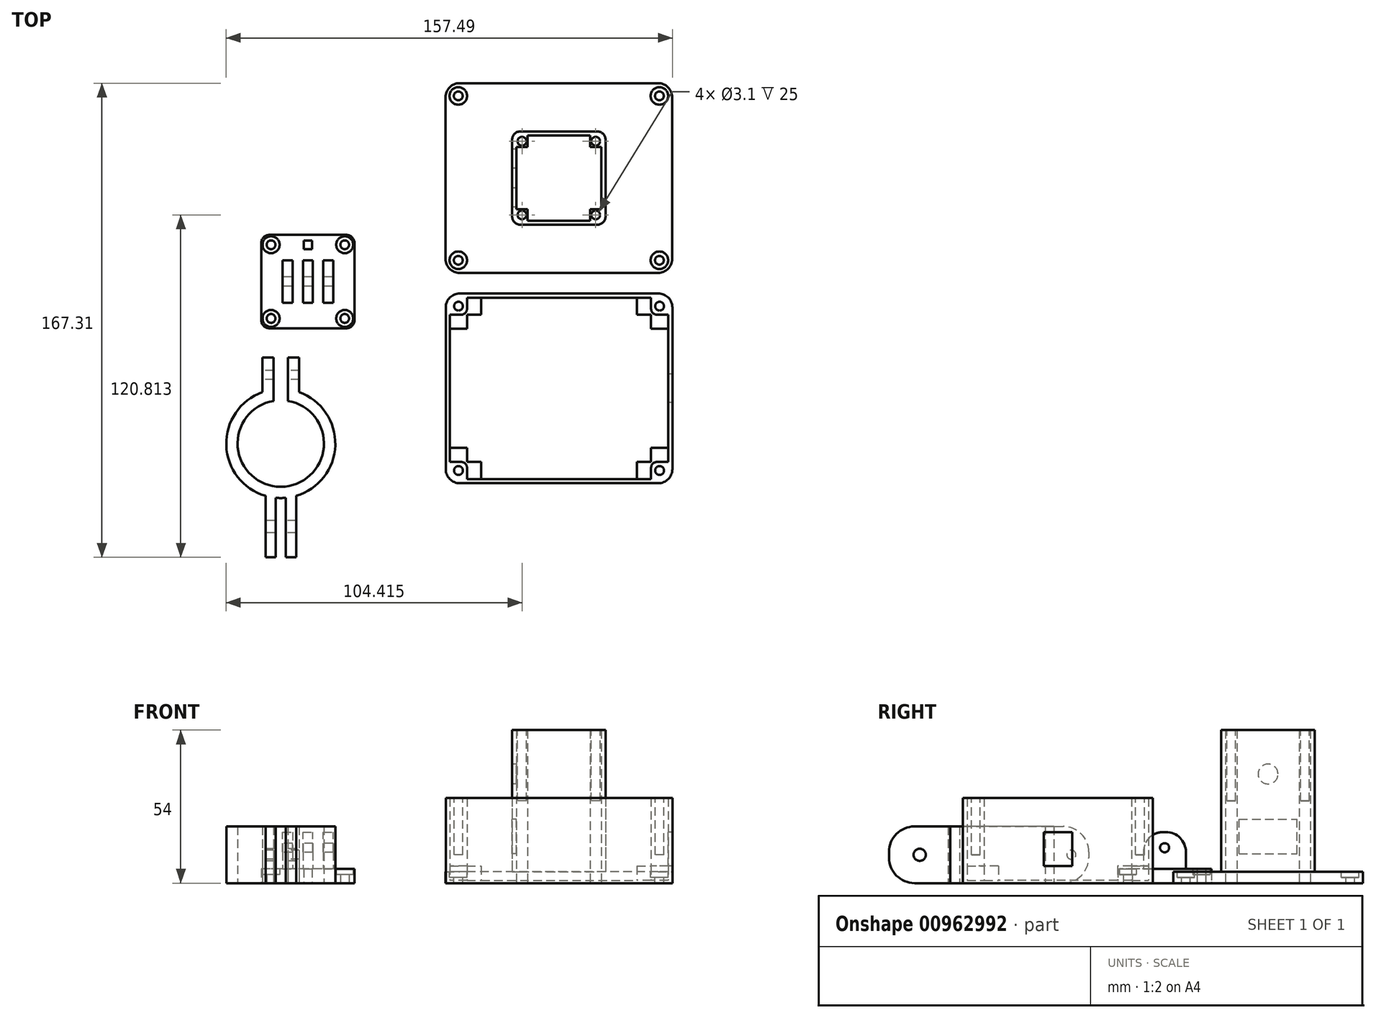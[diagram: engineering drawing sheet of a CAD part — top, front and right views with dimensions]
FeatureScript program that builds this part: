
annotation { "Feature Type Name" : "Feature", "Feature Type Description" : "" }
export const myFeature = defineFeature(function(context is Context, id is Id, definition is map)
    precondition{}
    {
        {
            var Q0;
            Q0=qCreatedBy(makeId("Top.planeOp"),FACE);
            var sketch = newSketch(context, id + "F0", { "sketchPlane" : qUnion([Q0])});
            skLineSegment(sketch, "E0.bottom", {"start": v(-40, 33.5) * mm, "end": v(40, 33.5) * mm});
            skLineSegment(sketch, "E0.top", {"start": v(-40, -33.5) * mm, "end": v(40, -33.5) * mm});
            skLineSegment(sketch, "E0.left", {"start": v(-40, 33.5) * mm, "end": v(-40, -33.5) * mm});
            skLineSegment(sketch, "E0.right", {"start": v(40, 33.5) * mm, "end": v(40, -33.5) * mm});
            skPoint(sketch, "E0.middle", {"position": v(0, 0) * mm});
            skSolve(sketch);
        }
        {
            var Q0;
            Q0 = qSketchRegion(id + "F0", true);
            extrude(context, id + "F1", {"entities" : qUnion([Q0]), "flatOperationType" : FlatOperationType.REMOVE, "depth" : 30 * mm, "offsetDistance" : 25 * mm, "domain" : OperationDomain.MODEL});
        }
        {
            var Q0;
            Q0=makeQuery(id+"F1.opExtrude","CAP_FACE",FACE,{"disambiguationData":[OSD([sQuery(id+"F0.wireOp",EDGE,"E0.bottom"),sQuery(id+"F0.wireOp",EDGE,"E0.top"),sQuery(id+"F0.wireOp",EDGE,"E0.left"),sQuery(id+"F0.wireOp",EDGE,"E0.right")])],"isStart":false});
            var sketch = newSketch(context, id + "F2", { "sketchPlane" : qUnion([Q0])});
            skLineSegment(sketch, "E1.bottom", {"start": v(-38.5, 32) * mm, "end": v(38.5, 32) * mm});
            skLineSegment(sketch, "E1.top", {"start": v(-38.5, -32) * mm, "end": v(38.5, -32) * mm});
            skLineSegment(sketch, "E1.left", {"start": v(-38.5, 32) * mm, "end": v(-38.5, -32) * mm});
            skLineSegment(sketch, "E1.right", {"start": v(38.5, 32) * mm, "end": v(38.5, -32) * mm});
            skPoint(sketch, "E1.middle", {"position": v(0, 0) * mm});
            skSolve(sketch);
        }
        {
            var Q0;
            Q0=makeQuery(id+"F2.imprint","IMPRINT",FACE,{"disambiguationData":[TD([[makeQuery(id+"F2.imprint","IMPRINT",EDGE,{"derivedFrom":sQuery(id+"F2.wireOp",EDGE,"E1.bottom")}),-1.0]])]});
            extrude(context, id + "F3", {"entities" : qUnion([Q0]), "operationType" : NewBodyOperationType.REMOVE, "oppositeDirection" : true, "depth" : 29 * mm, "offsetDistance" : 25 * mm});
        }
        {
            var Q0;
            Q0=makeQuery(id+"F3.boolean.opBoolean","COPY",FACE,{"derivedFrom":makeQuery(id+"F3.opExtrude","CAP_FACE",FACE,{"disambiguationData":[OSD([sQuery(id+"F2.wireOp",EDGE,"E1.bottom"),sQuery(id+"F2.wireOp",EDGE,"E1.top"),sQuery(id+"F2.wireOp",EDGE,"E1.left"),sQuery(id+"F2.wireOp",EDGE,"E1.right")])],"isStart":false})});
            var sketch = newSketch(context, id + "F4", { "sketchPlane" : qUnion([Q0])});
            skLineSegment(sketch, "E2.bottom", {"start": v(-38.5, 32) * mm, "end": v(-32.5, 32) * mm});
            skLineSegment(sketch, "E2.top", {"start": v(-38.5, 26) * mm, "end": v(-32.5, 26) * mm});
            skLineSegment(sketch, "E2.left", {"start": v(-38.5, 32) * mm, "end": v(-38.5, 26) * mm});
            skLineSegment(sketch, "E2.right", {"start": v(-32.5, 32) * mm, "end": v(-32.5, 26) * mm});
            skLineSegment(sketch, "E3.bottom", {"start": v(38.5, 32) * mm, "end": v(32.5, 32) * mm});
            skLineSegment(sketch, "E3.top", {"start": v(38.5, 26) * mm, "end": v(32.5, 26) * mm});
            skLineSegment(sketch, "E3.left", {"start": v(38.5, 32) * mm, "end": v(38.5, 26) * mm});
            skLineSegment(sketch, "E3.right", {"start": v(32.5, 32) * mm, "end": v(32.5, 26) * mm});
            skLineSegment(sketch, "E4.bottom", {"start": v(38.5, -32) * mm, "end": v(32.5, -32) * mm});
            skLineSegment(sketch, "E4.top", {"start": v(38.5, -26) * mm, "end": v(32.5, -26) * mm});
            skLineSegment(sketch, "E4.left", {"start": v(38.5, -32) * mm, "end": v(38.5, -26) * mm});
            skLineSegment(sketch, "E4.right", {"start": v(32.5, -32) * mm, "end": v(32.5, -26) * mm});
            skLineSegment(sketch, "E5.bottom", {"start": v(-38.5, -32) * mm, "end": v(-32.5, -32) * mm});
            skLineSegment(sketch, "E5.top", {"start": v(-38.5, -26) * mm, "end": v(-32.5, -26) * mm});
            skLineSegment(sketch, "E5.left", {"start": v(-38.5, -32) * mm, "end": v(-38.5, -26) * mm});
            skLineSegment(sketch, "E5.right", {"start": v(-32.5, -32) * mm, "end": v(-32.5, -26) * mm});
            skSolve(sketch);
        }
        {
            var Q0;
            Q0 = qSketchRegion(id + "F4", true);
            extrude(context, id + "F5", {"entities" : qUnion([Q0]), "operationType" : NewBodyOperationType.ADD, "depth" : 29 * mm, "offsetDistance" : 25 * mm});
        }
        {
            var Q0;
            Q0=makeQuery(id+"F5.boolean.opBoolean","MERGE",FACE,{"derivedFrom":[makeQuery(id+"F1.opExtrude","CAP_FACE",FACE,{"disambiguationData":[OSD([sQuery(id+"F0.wireOp",EDGE,"E0.bottom"),sQuery(id+"F0.wireOp",EDGE,"E0.top"),sQuery(id+"F0.wireOp",EDGE,"E0.left"),sQuery(id+"F0.wireOp",EDGE,"E0.right")])],"isStart":false}),makeQuery(id+"F5.opExtrude","CAP_FACE",FACE,{"disambiguationData":[OSD([sQuery(id+"F4.wireOp",EDGE,"E2.bottom"),sQuery(id+"F4.wireOp",EDGE,"E2.top"),sQuery(id+"F4.wireOp",EDGE,"E2.left"),sQuery(id+"F4.wireOp",EDGE,"E2.right")])],"isStart":false}),makeQuery(id+"F5.opExtrude","CAP_FACE",FACE,{"disambiguationData":[OSD([sQuery(id+"F4.wireOp",EDGE,"E3.bottom"),sQuery(id+"F4.wireOp",EDGE,"E3.top"),sQuery(id+"F4.wireOp",EDGE,"E3.left"),sQuery(id+"F4.wireOp",EDGE,"E3.right")])],"isStart":false}),makeQuery(id+"F5.opExtrude","CAP_FACE",FACE,{"disambiguationData":[OSD([sQuery(id+"F4.wireOp",EDGE,"E4.bottom"),sQuery(id+"F4.wireOp",EDGE,"E4.top"),sQuery(id+"F4.wireOp",EDGE,"E4.left"),sQuery(id+"F4.wireOp",EDGE,"E4.right")])],"isStart":false}),makeQuery(id+"F5.opExtrude","CAP_FACE",FACE,{"disambiguationData":[OSD([sQuery(id+"F4.wireOp",EDGE,"E5.bottom"),sQuery(id+"F4.wireOp",EDGE,"E5.top"),sQuery(id+"F4.wireOp",EDGE,"E5.left"),sQuery(id+"F4.wireOp",EDGE,"E5.right")])],"isStart":false})]});
            var sketch = newSketch(context, id + "F6", { "sketchPlane" : qUnion([Q0])});
            skCircle(sketch, "E6", {"center": v(35.5, 29) * mm, "radius": 1.55 * mm});
            skPoint(sketch, "E6.centerSnap0", {"position": v(32.5, 29) * mm});
            skPoint(sketch, "E6.centerSnap1", {"position": v(35.5, 26) * mm});
            skCircle(sketch, "E7", {"center": v(35.5, -29) * mm, "radius": 1.55 * mm});
            skPoint(sketch, "E7.centerSnap0", {"position": v(32.5, -29) * mm});
            skCircle(sketch, "E8", {"center": v(-35.5, -29) * mm, "radius": 1.55 * mm});
            skPoint(sketch, "E8.centerSnap0", {"position": v(-35.5, -26) * mm});
            skPoint(sketch, "E8.centerSnap1", {"position": v(-32.5, -29) * mm});
            skCircle(sketch, "E9", {"center": v(-35.5, 29) * mm, "radius": 1.55 * mm});
            skPoint(sketch, "E9.centerSnap0", {"position": v(-32.5, 29) * mm});
            skPoint(sketch, "E9.centerSnap1", {"position": v(-35.5, 26) * mm});
            skSolve(sketch);
        }
        {
            var Q0;
            Q0=makeQuery(id+"F6.imprint","IMPRINT",FACE,{"disambiguationData":[TD([[makeQuery(id+"F6.imprint","IMPRINT",EDGE,{"derivedFrom":sQuery(id+"F6.wireOp",EDGE,"E7")}),1.0]])]});
            var Q1;
            Q1=makeQuery(id+"F6.imprint","IMPRINT",FACE,{"disambiguationData":[TD([[makeQuery(id+"F6.imprint","IMPRINT",EDGE,{"derivedFrom":sQuery(id+"F6.wireOp",EDGE,"E8")}),1.0]])]});
            var Q2;
            Q2=makeQuery(id+"F6.imprint","IMPRINT",FACE,{"disambiguationData":[TD([[makeQuery(id+"F6.imprint","IMPRINT",EDGE,{"derivedFrom":sQuery(id+"F6.wireOp",EDGE,"E9")}),1.0]])]});
            var Q3;
            Q3=makeQuery(id+"F6.imprint","IMPRINT",FACE,{"disambiguationData":[TD([[makeQuery(id+"F6.imprint","IMPRINT",EDGE,{"derivedFrom":sQuery(id+"F6.wireOp",EDGE,"E6")}),1.0]])]});
            extrude(context, id + "F7", {"entities" : qUnion([Q0, Q1, Q2, Q3]), "operationType" : NewBodyOperationType.REMOVE, "oppositeDirection" : true, "depth" : 20 * mm, "offsetDistance" : 25 * mm});
        }
        {
            var Q0;
            Q0=makeQuery(id+"F3.boolean.opBoolean","COPY",FACE,{"derivedFrom":makeQuery(id+"F3.opExtrude","CAP_FACE",FACE,{"disambiguationData":[OSD([sQuery(id+"F2.wireOp",EDGE,"E1.bottom"),sQuery(id+"F2.wireOp",EDGE,"E1.top"),sQuery(id+"F2.wireOp",EDGE,"E1.left"),sQuery(id+"F2.wireOp",EDGE,"E1.right")])],"isStart":false})});
            var sketch = newSketch(context, id + "F8", { "sketchPlane" : qUnion([Q0])});
            skLineSegment(sketch, "E10.bottom", {"start": v(38.5, -26) * mm, "end": v(32.5, -26) * mm});
            skLineSegment(sketch, "E10.top", {"start": v(38.5, -21) * mm, "end": v(32.5, -21) * mm});
            skLineSegment(sketch, "E10.left", {"start": v(38.5, -26) * mm, "end": v(38.5, -21) * mm});
            skLineSegment(sketch, "E10.right", {"start": v(32.5, -26) * mm, "end": v(32.5, -21) * mm});
            skLineSegment(sketch, "E11.bottom", {"start": v(32.5, -32) * mm, "end": v(27.5, -32) * mm});
            skLineSegment(sketch, "E11.top", {"start": v(32.5, -26) * mm, "end": v(27.5, -26) * mm});
            skLineSegment(sketch, "E11.left", {"start": v(32.5, -32) * mm, "end": v(32.5, -26) * mm});
            skLineSegment(sketch, "E11.right", {"start": v(27.5, -32) * mm, "end": v(27.5, -26) * mm});
            skLineSegment(sketch, "E12.bottom", {"start": v(-32.5, -32) * mm, "end": v(-27.5, -32) * mm});
            skLineSegment(sketch, "E12.top", {"start": v(-32.5, -26) * mm, "end": v(-27.5, -26) * mm});
            skLineSegment(sketch, "E12.left", {"start": v(-32.5, -32) * mm, "end": v(-32.5, -26) * mm});
            skLineSegment(sketch, "E12.right", {"start": v(-27.5, -32) * mm, "end": v(-27.5, -26) * mm});
            skLineSegment(sketch, "E13.bottom", {"start": v(-32.5, -26) * mm, "end": v(-38.5, -26) * mm});
            skLineSegment(sketch, "E13.top", {"start": v(-32.5, -21) * mm, "end": v(-38.5, -21) * mm});
            skLineSegment(sketch, "E13.left", {"start": v(-32.5, -26) * mm, "end": v(-32.5, -21) * mm});
            skLineSegment(sketch, "E13.right", {"start": v(-38.5, -26) * mm, "end": v(-38.5, -21) * mm});
            skLineSegment(sketch, "E14.bottom", {"start": v(38.5, 26) * mm, "end": v(32.5, 26) * mm});
            skLineSegment(sketch, "E14.top", {"start": v(38.5, 21) * mm, "end": v(32.5, 21) * mm});
            skLineSegment(sketch, "E14.left", {"start": v(38.5, 26) * mm, "end": v(38.5, 21) * mm});
            skLineSegment(sketch, "E14.right", {"start": v(32.5, 26) * mm, "end": v(32.5, 21) * mm});
            skLineSegment(sketch, "E15.bottom", {"start": v(32.5, 26) * mm, "end": v(27.5, 26) * mm});
            skLineSegment(sketch, "E15.top", {"start": v(32.5, 32) * mm, "end": v(27.5, 32) * mm});
            skLineSegment(sketch, "E15.left", {"start": v(32.5, 26) * mm, "end": v(32.5, 32) * mm});
            skLineSegment(sketch, "E15.right", {"start": v(27.5, 26) * mm, "end": v(27.5, 32) * mm});
            skLineSegment(sketch, "E16.bottom", {"start": v(-32.5, 26) * mm, "end": v(-38.5, 26) * mm});
            skLineSegment(sketch, "E16.top", {"start": v(-32.5, 21) * mm, "end": v(-38.5, 21) * mm});
            skLineSegment(sketch, "E16.left", {"start": v(-32.5, 26) * mm, "end": v(-32.5, 21) * mm});
            skLineSegment(sketch, "E16.right", {"start": v(-38.5, 26) * mm, "end": v(-38.5, 21) * mm});
            skLineSegment(sketch, "E17.bottom", {"start": v(-32.5, 26) * mm, "end": v(-27.5, 26) * mm});
            skLineSegment(sketch, "E17.top", {"start": v(-32.5, 32) * mm, "end": v(-27.5, 32) * mm});
            skLineSegment(sketch, "E17.left", {"start": v(-32.5, 26) * mm, "end": v(-32.5, 32) * mm});
            skLineSegment(sketch, "E17.right", {"start": v(-27.5, 26) * mm, "end": v(-27.5, 32) * mm});
            skSolve(sketch);
        }
        {
            var Q0;
            Q0=makeQuery(id+"F8.imprint","IMPRINT",FACE,{"disambiguationData":[TD([[makeQuery(id+"F8.imprint","IMPRINT",EDGE,{"derivedFrom":sQuery(id+"F8.wireOp",EDGE,"E14.bottom")}),1.0]])]});
            var Q1;
            Q1=makeQuery(id+"F8.imprint","IMPRINT",FACE,{"disambiguationData":[TD([[makeQuery(id+"F8.imprint","IMPRINT",EDGE,{"derivedFrom":sQuery(id+"F8.wireOp",EDGE,"E15.bottom")}),-1.0]])]});
            var Q2;
            Q2=makeQuery(id+"F8.imprint","IMPRINT",FACE,{"disambiguationData":[TD([[makeQuery(id+"F8.imprint","IMPRINT",EDGE,{"derivedFrom":sQuery(id+"F8.wireOp",EDGE,"E10.bottom")}),-1.0]])]});
            var Q3;
            Q3=makeQuery(id+"F8.imprint","IMPRINT",FACE,{"disambiguationData":[TD([[makeQuery(id+"F8.imprint","IMPRINT",EDGE,{"derivedFrom":sQuery(id+"F8.wireOp",EDGE,"E11.bottom")}),1.0]])]});
            var Q4;
            Q4=makeQuery(id+"F8.imprint","IMPRINT",FACE,{"disambiguationData":[TD([[makeQuery(id+"F8.imprint","IMPRINT",EDGE,{"derivedFrom":sQuery(id+"F8.wireOp",EDGE,"E12.bottom")}),1.0]])]});
            var Q5;
            Q5=makeQuery(id+"F8.imprint","IMPRINT",FACE,{"disambiguationData":[TD([[makeQuery(id+"F8.imprint","IMPRINT",EDGE,{"derivedFrom":sQuery(id+"F8.wireOp",EDGE,"E13.bottom")}),1.0]])]});
            var Q6;
            Q6=makeQuery(id+"F8.imprint","IMPRINT",FACE,{"disambiguationData":[TD([[makeQuery(id+"F8.imprint","IMPRINT",EDGE,{"derivedFrom":sQuery(id+"F8.wireOp",EDGE,"E16.bottom")}),-1.0]])]});
            var Q7;
            Q7=makeQuery(id+"F8.imprint","IMPRINT",FACE,{"disambiguationData":[TD([[makeQuery(id+"F8.imprint","IMPRINT",EDGE,{"derivedFrom":sQuery(id+"F8.wireOp",EDGE,"E17.bottom")}),1.0]])]});
            extrude(context, id + "F9", {"entities" : qUnion([Q0, Q1, Q2, Q3, Q4, Q5, Q6, Q7]), "operationType" : NewBodyOperationType.ADD, "depth" : 5 * mm, "offsetDistance" : 25 * mm});
        }
        {
            var Q0;
            Q0=makeQuery(id+"F3.boolean.opBoolean","COPY",FACE,{"derivedFrom":makeQuery(id+"F3.opExtrude","SWEPT_FACE",FACE,{"disambiguationData":[OSD([sQuery(id+"F2.wireOp",EDGE,"E1.right")])]})});
            var sketch = newSketch(context, id + "F10", { "sketchPlane" : qUnion([Q0])});
            skPoint(sketch, "E18.middle.positionSnap0", {"position": v(0, 1) * mm});
            skPoint(sketch, "E18.centerSnap0", {"position": v(0, 1) * mm});
            skPoint(sketch, "E19", {"position": v(-26, 12) * mm});
            skLineSegment(sketch, "E20.bottom", {"start": v(-5, 6) * mm, "end": v(5, 6) * mm});
            skLineSegment(sketch, "E20.top", {"start": v(-5, 18) * mm, "end": v(5, 18) * mm});
            skLineSegment(sketch, "E20.left", {"start": v(-5, 6) * mm, "end": v(-5, 18) * mm});
            skLineSegment(sketch, "E20.right", {"start": v(5, 6) * mm, "end": v(5, 18) * mm});
            skPoint(sketch, "E20.middle", {"position": v(0, 12) * mm});
            skSolve(sketch);
        }
        {
            var Q0;
            Q0=makeQuery(id+"F10.imprint","IMPRINT",FACE,{"disambiguationData":[TD([[makeQuery(id+"F10.imprint","IMPRINT",EDGE,{"derivedFrom":sQuery(id+"F10.wireOp",EDGE,"E20.bottom")}),1.0]])]});
            extrude(context, id + "F11", {"entities" : qUnion([Q0]), "operationType" : NewBodyOperationType.REMOVE, "oppositeDirection" : true, "depth" : 25 * mm, "offsetDistance" : 25 * mm});
        }
        {
            var Q0;
            Q0=makeQuery(id+"F10.imprint","IMPRINT",FACE,{"disambiguationData":[TD([[makeQuery(id+"F10.imprint","IMPRINT",EDGE,{"derivedFrom":sQuery(id+"F10.wireOp",EDGE,"E20.bottom")}),1.0]])]});
            extrude(context, id + "F12", {"entities" : qUnion([Q0]), "operationType" : NewBodyOperationType.REMOVE, "oppositeDirection" : true, "depth" : 25 * mm, "offsetDistance" : 25 * mm});
        }
        {
            var Q0;
            Q0=qCreatedBy(makeId("Top.planeOp"),FACE);
            var sketch = newSketch(context, id + "F13", { "sketchPlane" : qUnion([Q0])});
            skLineSegment(sketch, "E21.bottom", {"start": v(39.93, 40.7) * mm, "end": v(-40.07, 40.7) * mm});
            skLineSegment(sketch, "E21.top", {"start": v(39.93, 107.7) * mm, "end": v(-40.07, 107.7) * mm});
            skLineSegment(sketch, "E21.left", {"start": v(39.93, 40.7) * mm, "end": v(39.93, 107.7) * mm});
            skLineSegment(sketch, "E21.right", {"start": v(-40.07, 40.7) * mm, "end": v(-40.07, 107.7) * mm});
            skSolve(sketch);
        }
        {
            var Q0;
            Q0=makeQuery(id+"F13.imprint","IMPRINT",FACE,{"disambiguationData":[TD([[makeQuery(id+"F13.imprint","IMPRINT",EDGE,{"derivedFrom":sQuery(id+"F13.wireOp",EDGE,"E21.bottom")}),-1.0]])]});
            var Q1;
            Q1 = qSketchRegion(id + "F15", true);
            extrude(context, id + "F14", {"entities" : qUnion([Q0, Q1]), "depth" : 4 * mm, "offsetDistance" : 25 * mm});
        }
        {
            var Q0;
            Q0=makeQuery(id+"F14.opExtrude","CAP_FACE",FACE,{"disambiguationData":[OSD([sQuery(id+"F13.wireOp",EDGE,"E21.bottom"),sQuery(id+"F13.wireOp",EDGE,"E21.top"),sQuery(id+"F13.wireOp",EDGE,"E21.left"),sQuery(id+"F13.wireOp",EDGE,"E21.right")])],"isStart":false});
            var sketch = newSketch(context, id + "F15", { "sketchPlane" : qUnion([Q0])});
            skCircle(sketch, "E22", {"center": v(35.43, 45.2) * mm, "radius": 1.55 * mm});
            skCircle(sketch, "E23", {"center": v(-35.57, 45.2) * mm, "radius": 1.55 * mm});
            skCircle(sketch, "E24", {"center": v(-35.57, 103.2) * mm, "radius": 1.55 * mm});
            skCircle(sketch, "E25", {"center": v(35.43, 103.2) * mm, "radius": 1.55 * mm});
            skSolve(sketch);
        }
        {
            var Q0;
            Q0 = qSketchRegion(id + "F15", true);
            extrude(context, id + "F16", {"entities" : qUnion([Q0]), "operationType" : NewBodyOperationType.REMOVE, "oppositeDirection" : true, "depth" : 25 * mm, "offsetDistance" : 25 * mm});
        }
        {
            var Q0;
            Q0=makeQuery(id+"F14.opExtrude","CAP_FACE",FACE,{"disambiguationData":[OSD([sQuery(id+"F13.wireOp",EDGE,"E21.bottom"),sQuery(id+"F13.wireOp",EDGE,"E21.top"),sQuery(id+"F13.wireOp",EDGE,"E21.left"),sQuery(id+"F13.wireOp",EDGE,"E21.right")])],"isStart":false});
            var sketch = newSketch(context, id + "F17", { "sketchPlane" : qUnion([Q0])});
            skCircle(sketch, "E26", {"center": v(35.43, 45.2) * mm, "radius": 3.1 * mm});
            skCircle(sketch, "E27", {"center": v(-35.57, 45.2) * mm, "radius": 3.1 * mm});
            skCircle(sketch, "E28", {"center": v(-35.57, 103.2) * mm, "radius": 3.1 * mm});
            skCircle(sketch, "E29", {"center": v(35.43, 103.2) * mm, "radius": 3.1 * mm});
            skSolve(sketch);
        }
        {
            var Q0;
            Q0 = qSketchRegion(id + "F17", true);
            extrude(context, id + "F18", {"entities" : qUnion([Q0]), "operationType" : NewBodyOperationType.REMOVE, "oppositeDirection" : true, "depth" : 2 * mm, "offsetDistance" : 25 * mm});
        }
        {
            var Q0;
            Q0=makeQuery(id+"F5.opExtrude","SWEPT_EDGE",EDGE,{"disambiguationData":[OSD([sQuery(id+"F4.wireOp",EDGE,"E4.top"),sQuery(id+"F4.wireOp",EDGE,"E4.right")])]});
            var Q1;
            Q1=makeQuery(id+"F5.opExtrude","SWEPT_EDGE",EDGE,{"disambiguationData":[OSD([sQuery(id+"F4.wireOp",EDGE,"E5.top"),sQuery(id+"F4.wireOp",EDGE,"E5.right")])]});
            var Q2;
            Q2=makeQuery(id+"F5.opExtrude","SWEPT_EDGE",EDGE,{"disambiguationData":[OSD([sQuery(id+"F4.wireOp",EDGE,"E2.top"),sQuery(id+"F4.wireOp",EDGE,"E2.right")])]});
            var Q3;
            Q3=makeQuery(id+"F5.opExtrude","SWEPT_EDGE",EDGE,{"disambiguationData":[OSD([sQuery(id+"F4.wireOp",EDGE,"E3.top"),sQuery(id+"F4.wireOp",EDGE,"E3.right")])]});
            fillet(context, id + "F19", {"entities" : qUnion([Q0, Q1, Q2, Q3]), "radius" : 2 * mm, "tangentPropagation" : true, "allowEdgeOverflow" : false});
        }
        {
            var Q0;
            Q0=makeQuery(id+"F1.opExtrude","SWEPT_EDGE",EDGE,{"disambiguationData":[OSD([sQuery(id+"F0.wireOp",EDGE,"E0.top"),sQuery(id+"F0.wireOp",EDGE,"E0.right")])]});
            var Q1;
            Q1=makeQuery(id+"F1.opExtrude","SWEPT_EDGE",EDGE,{"disambiguationData":[OSD([sQuery(id+"F0.wireOp",EDGE,"E0.top"),sQuery(id+"F0.wireOp",EDGE,"E0.left")])]});
            var Q2;
            Q2=makeQuery(id+"F1.opExtrude","SWEPT_EDGE",EDGE,{"disambiguationData":[OSD([sQuery(id+"F0.wireOp",EDGE,"E0.bottom"),sQuery(id+"F0.wireOp",EDGE,"E0.left")])]});
            var Q3;
            Q3=makeQuery(id+"F1.opExtrude","SWEPT_EDGE",EDGE,{"disambiguationData":[OSD([sQuery(id+"F0.wireOp",EDGE,"E0.bottom"),sQuery(id+"F0.wireOp",EDGE,"E0.right")])]});
            fillet(context, id + "F20", {"entities" : qUnion([Q0, Q1, Q2, Q3]), "radius" : 5 * mm, "tangentPropagation" : true, "allowEdgeOverflow" : false});
        }
        {
            var Q0;
            Q0=makeQuery(id+"F14.opExtrude","SWEPT_EDGE",EDGE,{"disambiguationData":[OSD([sQuery(id+"F13.wireOp",EDGE,"E21.bottom"),sQuery(id+"F13.wireOp",EDGE,"E21.left")])]});
            var Q1;
            Q1=makeQuery(id+"F14.opExtrude","SWEPT_EDGE",EDGE,{"disambiguationData":[OSD([sQuery(id+"F13.wireOp",EDGE,"E21.top"),sQuery(id+"F13.wireOp",EDGE,"E21.left")])]});
            var Q2;
            Q2=makeQuery(id+"F14.opExtrude","SWEPT_EDGE",EDGE,{"disambiguationData":[OSD([sQuery(id+"F13.wireOp",EDGE,"E21.top"),sQuery(id+"F13.wireOp",EDGE,"E21.right")])]});
            var Q3;
            Q3=makeQuery(id+"F14.opExtrude","SWEPT_EDGE",EDGE,{"disambiguationData":[OSD([sQuery(id+"F13.wireOp",EDGE,"E21.bottom"),sQuery(id+"F13.wireOp",EDGE,"E21.right")])]});
            fillet(context, id + "F21", {"entities" : qUnion([Q0, Q1, Q2, Q3]), "radius" : 5 * mm, "tangentPropagation" : true, "allowEdgeOverflow" : false});
        }
        {
            var Q0;
            Q0=makeQuery(id+"F14.opExtrude","CAP_FACE",FACE,{"disambiguationData":[OSD([sQuery(id+"F13.wireOp",EDGE,"E21.bottom"),sQuery(id+"F13.wireOp",EDGE,"E21.top"),sQuery(id+"F13.wireOp",EDGE,"E21.left"),sQuery(id+"F13.wireOp",EDGE,"E21.right")])],"isStart":false});
            var sketch = newSketch(context, id + "F22", { "sketchPlane" : qUnion([Q0])});
            skLineSegment(sketch, "E30.bottom", {"start": v(-15.07, 89.2) * mm, "end": v(14.93, 89.2) * mm});
            skLineSegment(sketch, "E30.top", {"start": v(-15.07, 59.2) * mm, "end": v(14.93, 59.2) * mm});
            skLineSegment(sketch, "E30.left", {"start": v(-15.07, 89.2) * mm, "end": v(-15.07, 59.2) * mm});
            skLineSegment(sketch, "E30.right", {"start": v(14.93, 89.2) * mm, "end": v(14.93, 59.2) * mm});
            skPoint(sketch, "E30.middle", {"position": v(-0.07, 74.2) * mm});
            skPoint(sketch, "E30.middle.positionSnap0", {"position": v(-0.07, 40.7) * mm});
            skPoint(sketch, "E30.middle.positionSnap1", {"position": v(-40.07, 74.2) * mm});
            skPoint(sketch, "E30.centerSnap0", {"position": v(-0.07, 40.7) * mm});
            skPoint(sketch, "E30.centerSnap1", {"position": v(-40.07, 74.2) * mm});
            skLineSegment(sketch, "E31.bottom", {"start": v(-16.57, 57.7) * mm, "end": v(16.43, 57.7) * mm});
            skLineSegment(sketch, "E31.top", {"start": v(-16.57, 90.7) * mm, "end": v(16.43, 90.7) * mm});
            skLineSegment(sketch, "E31.left", {"start": v(-16.57, 57.7) * mm, "end": v(-16.57, 90.7) * mm});
            skLineSegment(sketch, "E31.right", {"start": v(16.43, 57.7) * mm, "end": v(16.43, 90.7) * mm});
            skSolve(sketch);
        }
        {
            var Q0;
            Q0=makeQuery(id+"F22.imprint","IMPRINT",FACE,{"disambiguationData":[TD([[makeQuery(id+"F22.imprint","IMPRINT",EDGE,{"derivedFrom":sQuery(id+"F22.wireOp",EDGE,"E30.bottom")}),-1.0]])]});
            extrude(context, id + "F23", {"entities" : qUnion([Q0]), "operationType" : NewBodyOperationType.REMOVE, "oppositeDirection" : true, "depth" : 25 * mm, "offsetDistance" : 25 * mm});
        }
        {
            var Q0;
            Q0 = qSketchRegion(id + "F22", true);
            extrude(context, id + "F24", {"entities" : qUnion([Q0]), "operationType" : NewBodyOperationType.ADD, "depth" : 50 * mm, "offsetDistance" : 25 * mm});
        }
        {
            var Q0;
            Q0=makeQuery(id+"F14.opExtrude","CAP_FACE",FACE,{"disambiguationData":[OSD([sQuery(id+"F13.wireOp",EDGE,"E21.bottom"),sQuery(id+"F13.wireOp",EDGE,"E21.top"),sQuery(id+"F13.wireOp",EDGE,"E21.left"),sQuery(id+"F13.wireOp",EDGE,"E21.right")])],"isStart":true});
            var sketch = newSketch(context, id + "F25", { "sketchPlane" : qUnion([Q0])});
            skLineSegment(sketch, "E32.bottom", {"start": v(14.93, -89.2) * mm, "end": v(10.93, -89.2) * mm});
            skLineSegment(sketch, "E32.top", {"start": v(14.93, -85.2) * mm, "end": v(10.93, -85.2) * mm});
            skLineSegment(sketch, "E32.left", {"start": v(14.93, -89.2) * mm, "end": v(14.93, -85.2) * mm});
            skLineSegment(sketch, "E32.right", {"start": v(10.93, -89.2) * mm, "end": v(10.93, -85.2) * mm});
            skLineSegment(sketch, "E33.bottom", {"start": v(-15.07, -89.2) * mm, "end": v(-11.07, -89.2) * mm});
            skLineSegment(sketch, "E33.top", {"start": v(-15.07, -85.2) * mm, "end": v(-11.07, -85.2) * mm});
            skLineSegment(sketch, "E33.left", {"start": v(-15.07, -89.2) * mm, "end": v(-15.07, -85.2) * mm});
            skLineSegment(sketch, "E33.right", {"start": v(-11.07, -89.2) * mm, "end": v(-11.07, -85.2) * mm});
            skLineSegment(sketch, "E34.bottom", {"start": v(-15.07, -59.2) * mm, "end": v(-11.07, -59.2) * mm});
            skLineSegment(sketch, "E34.top", {"start": v(-15.07, -63.2) * mm, "end": v(-11.07, -63.2) * mm});
            skLineSegment(sketch, "E34.left", {"start": v(-15.07, -59.2) * mm, "end": v(-15.07, -63.2) * mm});
            skLineSegment(sketch, "E34.right", {"start": v(-11.07, -59.2) * mm, "end": v(-11.07, -63.2) * mm});
            skLineSegment(sketch, "E35.bottom", {"start": v(14.93, -59.2) * mm, "end": v(10.93, -59.2) * mm});
            skLineSegment(sketch, "E35.top", {"start": v(14.93, -63.2) * mm, "end": v(10.93, -63.2) * mm});
            skLineSegment(sketch, "E35.left", {"start": v(14.93, -59.2) * mm, "end": v(14.93, -63.2) * mm});
            skLineSegment(sketch, "E35.right", {"start": v(10.93, -59.2) * mm, "end": v(10.93, -63.2) * mm});
            skSolve(sketch);
        }
        {
            var Q0;
            Q0=makeQuery(id+"F25.imprint","IMPRINT",FACE,{"disambiguationData":[TD([[makeQuery(id+"F25.imprint","IMPRINT",EDGE,{"derivedFrom":sQuery(id+"F25.wireOp",EDGE,"E35.bottom")}),-1.0]])]});
            var Q1;
            Q1=makeQuery(id+"F25.imprint","IMPRINT",FACE,{"disambiguationData":[TD([[makeQuery(id+"F25.imprint","IMPRINT",EDGE,{"derivedFrom":sQuery(id+"F25.wireOp",EDGE,"E34.bottom")}),-1.0]])]});
            var Q2;
            Q2=makeQuery(id+"F25.imprint","IMPRINT",FACE,{"disambiguationData":[TD([[makeQuery(id+"F25.imprint","IMPRINT",EDGE,{"derivedFrom":sQuery(id+"F25.wireOp",EDGE,"E33.bottom")}),1.0]])]});
            var Q3;
            Q3=makeQuery(id+"F25.imprint","IMPRINT",FACE,{"disambiguationData":[TD([[makeQuery(id+"F25.imprint","IMPRINT",EDGE,{"derivedFrom":sQuery(id+"F25.wireOp",EDGE,"E32.bottom")}),1.0]])]});
            extrude(context, id + "F26", {"entities" : qUnion([Q0, Q1, Q2, Q3]), "operationType" : NewBodyOperationType.ADD, "oppositeDirection" : true, "depth" : 54 * mm, "offsetDistance" : 25 * mm});
        }
        {
            var Q0;
            Q0=makeQuery(id+"F26.boolean.opBoolean","MERGE",FACE,{"derivedFrom":[makeQuery(id+"F24.opExtrude","CAP_FACE",FACE,{"disambiguationData":[OSD([sQuery(id+"F22.wireOp",EDGE,"E30.bottom"),sQuery(id+"F22.wireOp",EDGE,"E30.top"),sQuery(id+"F22.wireOp",EDGE,"E30.left"),sQuery(id+"F22.wireOp",EDGE,"E30.right"),sQuery(id+"F22.wireOp",EDGE,"E31.bottom"),sQuery(id+"F22.wireOp",EDGE,"E31.top"),sQuery(id+"F22.wireOp",EDGE,"E31.left"),sQuery(id+"F22.wireOp",EDGE,"E31.right")])],"isStart":false}),makeQuery(id+"F26.opExtrude","CAP_FACE",FACE,{"disambiguationData":[OSD([sQuery(id+"F25.wireOp",EDGE,"E32.bottom"),sQuery(id+"F25.wireOp",EDGE,"E32.top"),sQuery(id+"F25.wireOp",EDGE,"E32.left"),sQuery(id+"F25.wireOp",EDGE,"E32.right")])],"isStart":false}),makeQuery(id+"F26.opExtrude","CAP_FACE",FACE,{"disambiguationData":[OSD([sQuery(id+"F25.wireOp",EDGE,"E33.bottom"),sQuery(id+"F25.wireOp",EDGE,"E33.top"),sQuery(id+"F25.wireOp",EDGE,"E33.left"),sQuery(id+"F25.wireOp",EDGE,"E33.right")])],"isStart":false}),makeQuery(id+"F26.opExtrude","CAP_FACE",FACE,{"disambiguationData":[OSD([sQuery(id+"F25.wireOp",EDGE,"E34.bottom"),sQuery(id+"F25.wireOp",EDGE,"E34.top"),sQuery(id+"F25.wireOp",EDGE,"E34.left"),sQuery(id+"F25.wireOp",EDGE,"E34.right")])],"isStart":false}),makeQuery(id+"F26.opExtrude","CAP_FACE",FACE,{"disambiguationData":[OSD([sQuery(id+"F25.wireOp",EDGE,"E35.bottom"),sQuery(id+"F25.wireOp",EDGE,"E35.top"),sQuery(id+"F25.wireOp",EDGE,"E35.left"),sQuery(id+"F25.wireOp",EDGE,"E35.right")])],"isStart":false})]});
            var sketch = newSketch(context, id + "F27", { "sketchPlane" : qUnion([Q0])});
            skCircle(sketch, "E36", {"center": v(12.93, 61.2) * mm, "radius": 1.55 * mm});
            skPoint(sketch, "E36.centerSnap0", {"position": v(12.93, 63.2) * mm});
            skPoint(sketch, "E36.centerSnap1", {"position": v(10.93, 61.2) * mm});
            skCircle(sketch, "E37", {"center": v(-13.07, 61.2) * mm, "radius": 1.55 * mm});
            skPoint(sketch, "E37.centerSnap0", {"position": v(-11.07, 61.2) * mm});
            skPoint(sketch, "E37.centerSnap1", {"position": v(-13.07, 63.2) * mm});
            skCircle(sketch, "E38", {"center": v(-13.07, 87.2) * mm, "radius": 1.55 * mm});
            skPoint(sketch, "E38.centerSnap0", {"position": v(-11.07, 87.2) * mm});
            skPoint(sketch, "E38.centerSnap1", {"position": v(-13.07, 85.2) * mm});
            skCircle(sketch, "E39", {"center": v(12.93, 87.2) * mm, "radius": 1.55 * mm});
            skPoint(sketch, "E39.centerSnap0", {"position": v(10.93, 87.2) * mm});
            skPoint(sketch, "E39.centerSnap1", {"position": v(12.93, 85.2) * mm});
            skSolve(sketch);
        }
        {
            var Q0;
            Q0=makeQuery(id+"F27.imprint","IMPRINT",FACE,{"disambiguationData":[TD([[makeQuery(id+"F27.imprint","IMPRINT",EDGE,{"derivedFrom":sQuery(id+"F27.wireOp",EDGE,"E36")}),1.0]])]});
            var Q1;
            Q1=makeQuery(id+"F27.imprint","IMPRINT",FACE,{"disambiguationData":[TD([[makeQuery(id+"F27.imprint","IMPRINT",EDGE,{"derivedFrom":sQuery(id+"F27.wireOp",EDGE,"E37")}),1.0]])]});
            var Q2;
            Q2=makeQuery(id+"F27.imprint","IMPRINT",FACE,{"disambiguationData":[TD([[makeQuery(id+"F27.imprint","IMPRINT",EDGE,{"derivedFrom":sQuery(id+"F27.wireOp",EDGE,"E38")}),1.0]])]});
            var Q3;
            Q3=makeQuery(id+"F27.imprint","IMPRINT",FACE,{"disambiguationData":[TD([[makeQuery(id+"F27.imprint","IMPRINT",EDGE,{"derivedFrom":sQuery(id+"F27.wireOp",EDGE,"E39")}),1.0]])]});
            extrude(context, id + "F28", {"entities" : qUnion([Q0, Q1, Q2, Q3]), "operationType" : NewBodyOperationType.REMOVE, "oppositeDirection" : true, "depth" : 25 * mm, "offsetDistance" : 25 * mm});
        }
        {
            var Q0;
            Q0=makeQuery(id+"F24.opExtrude","SWEPT_EDGE",EDGE,{"disambiguationData":[OSD([sQuery(id+"F22.wireOp",EDGE,"E31.top"),sQuery(id+"F22.wireOp",EDGE,"E31.left")])]});
            var Q1;
            Q1=makeQuery(id+"F24.opExtrude","SWEPT_EDGE",EDGE,{"disambiguationData":[OSD([sQuery(id+"F22.wireOp",EDGE,"E31.bottom"),sQuery(id+"F22.wireOp",EDGE,"E31.left")])]});
            var Q2;
            Q2=makeQuery(id+"F24.opExtrude","SWEPT_EDGE",EDGE,{"disambiguationData":[OSD([sQuery(id+"F22.wireOp",EDGE,"E31.top"),sQuery(id+"F22.wireOp",EDGE,"E31.right")])]});
            var Q3;
            Q3=makeQuery(id+"F24.opExtrude","SWEPT_EDGE",EDGE,{"disambiguationData":[OSD([sQuery(id+"F22.wireOp",EDGE,"E31.bottom"),sQuery(id+"F22.wireOp",EDGE,"E31.right")])]});
            fillet(context, id + "F29", {"entities" : qUnion([Q0, Q1, Q2, Q3]), "radius" : 3 * mm, "tangentPropagation" : true, "allowEdgeOverflow" : false});
        }
        {
            var Q0;
            Q0=makeQuery(id+"F24.opExtrude","SWEPT_FACE",FACE,{"disambiguationData":[OSD([sQuery(id+"F22.wireOp",EDGE,"E31.left")])]});
            var sketch = newSketch(context, id + "F30", { "sketchPlane" : qUnion([Q0])});
            skCircle(sketch, "E40", {"center": v(-74.2, 38.5) * mm, "radius": 3.5 * mm});
            skPoint(sketch, "E40.centerSnap0", {"position": v(-74.2, 54) * mm});
            skLineSegment(sketch, "E41.bottom", {"start": v(-63.94, 10.4) * mm, "end": v(-84.44, 10.4) * mm});
            skLineSegment(sketch, "E41.top", {"start": v(-63.94, 22.5) * mm, "end": v(-84.44, 22.5) * mm});
            skLineSegment(sketch, "E41.left", {"start": v(-63.94, 10.4) * mm, "end": v(-63.94, 22.5) * mm});
            skLineSegment(sketch, "E41.right", {"start": v(-84.44, 10.4) * mm, "end": v(-84.44, 22.5) * mm});
            skPoint(sketch, "E41.middle", {"position": v(-74.2, 16.45) * mm});
            skSolve(sketch);
        }
        {
            var Q0;
            Q0=makeQuery(id+"F30.imprint","IMPRINT",FACE,{"disambiguationData":[TD([[makeQuery(id+"F30.imprint","IMPRINT",EDGE,{"derivedFrom":sQuery(id+"F30.wireOp",EDGE,"E41.bottom")}),-1.0]])]});
            var Q1;
            Q1=makeQuery(id+"F30.imprint","IMPRINT",FACE,{"disambiguationData":[TD([[makeQuery(id+"F30.imprint","IMPRINT",EDGE,{"derivedFrom":sQuery(id+"F30.wireOp",EDGE,"E40")}),1.0]])]});
            extrude(context, id + "F31", {"entities" : qUnion([Q0, Q1]), "operationType" : NewBodyOperationType.REMOVE, "oppositeDirection" : true, "depth" : 25 * mm, "offsetDistance" : 25 * mm});
        }
        {
            var Q0;
            Q0=qCreatedBy(makeId("Top.planeOp"),FACE);
            var sketch = newSketch(context, id + "F32", { "sketchPlane" : qUnion([Q0])});
            skLineSegment(sketch, "E42.bottom", {"start": v(-72.17, 54.17) * mm, "end": v(-105.17, 54.17) * mm});
            skLineSegment(sketch, "E42.top", {"start": v(-72.17, 21.17) * mm, "end": v(-105.17, 21.17) * mm});
            skLineSegment(sketch, "E42.left", {"start": v(-72.17, 54.17) * mm, "end": v(-72.17, 21.17) * mm});
            skLineSegment(sketch, "E42.right", {"start": v(-105.17, 54.17) * mm, "end": v(-105.17, 21.17) * mm});
            skCircle(sketch, "E43", {"center": v(-75.67, 50.67) * mm, "radius": 1.55 * mm});
            skCircle(sketch, "E44", {"center": v(-75.67, 24.67) * mm, "radius": 1.55 * mm});
            skCircle(sketch, "E45", {"center": v(-101.67, 24.67) * mm, "radius": 1.55 * mm});
            skCircle(sketch, "E46", {"center": v(-101.67, 50.67) * mm, "radius": 1.55 * mm});
            skLineSegment(sketch, "E47.bottom", {"start": v(-90.17, 49.17) * mm, "end": v(-87.17, 49.17) * mm});
            skLineSegment(sketch, "E47.top", {"start": v(-90.17, 52.17) * mm, "end": v(-87.17, 52.17) * mm});
            skLineSegment(sketch, "E47.left", {"start": v(-90.17, 49.17) * mm, "end": v(-90.17, 52.17) * mm});
            skLineSegment(sketch, "E47.right", {"start": v(-87.17, 49.17) * mm, "end": v(-87.17, 52.17) * mm});
            skPoint(sketch, "E47.middle", {"position": v(-88.67, 50.67) * mm});
            skPoint(sketch, "E47.middle.positionSnap0", {"position": v(-88.67, 54.17) * mm});
            skPoint(sketch, "E47.centerSnap0", {"position": v(-88.67, 54.17) * mm});
            skLineSegment(sketch, "E48.bottom", {"start": v(-97.62, 30.17) * mm, "end": v(-79.72, 30.17) * mm});
            skLineSegment(sketch, "E48.top", {"start": v(-97.62, 45.17) * mm, "end": v(-79.72, 45.17) * mm});
            skLineSegment(sketch, "E48.left", {"start": v(-97.62, 30.17) * mm, "end": v(-97.62, 45.17) * mm});
            skLineSegment(sketch, "E48.right", {"start": v(-79.72, 30.17) * mm, "end": v(-79.72, 45.17) * mm});
            skPoint(sketch, "E48.middle", {"position": v(-88.67, 37.67) * mm});
            skPoint(sketch, "E48.middle.positionSnap0", {"position": v(-88.67, 21.17) * mm});
            skPoint(sketch, "E48.middle.positionSnap1", {"position": v(-72.17, 37.67) * mm});
            skPoint(sketch, "E48.centerSnap0", {"position": v(-88.67, 21.17) * mm});
            skPoint(sketch, "E48.centerSnap1", {"position": v(-72.17, 37.67) * mm});
            skCircle(sketch, "E49", {"center": v(-75.67, 50.67) * mm, "radius": 3 * mm});
            skCircle(sketch, "E50", {"center": v(-75.67, 24.67) * mm, "radius": 3 * mm});
            skCircle(sketch, "E51", {"center": v(-101.67, 24.67) * mm, "radius": 3 * mm});
            skCircle(sketch, "E52", {"center": v(-101.67, 50.67) * mm, "radius": 3 * mm});
            skLineSegment(sketch, "E53.bottom", {"start": v(-86.92, 30.17) * mm, "end": v(-90.42, 30.17) * mm});
            skLineSegment(sketch, "E53.top", {"start": v(-86.92, 45.17) * mm, "end": v(-90.42, 45.17) * mm});
            skLineSegment(sketch, "E53.left", {"start": v(-86.92, 30.17) * mm, "end": v(-86.92, 45.17) * mm});
            skLineSegment(sketch, "E53.right", {"start": v(-90.42, 30.17) * mm, "end": v(-90.42, 45.17) * mm});
            skLineSegment(sketch, "E54.bottom", {"start": v(-97.62, 45.17) * mm, "end": v(-94.12, 45.17) * mm});
            skLineSegment(sketch, "E54.top", {"start": v(-97.62, 30.17) * mm, "end": v(-94.12, 30.17) * mm});
            skLineSegment(sketch, "E54.left", {"start": v(-97.62, 45.17) * mm, "end": v(-97.62, 30.17) * mm});
            skLineSegment(sketch, "E54.right", {"start": v(-94.12, 45.17) * mm, "end": v(-94.12, 30.17) * mm});
            skLineSegment(sketch, "E55.bottom", {"start": v(-79.72, 30.17) * mm, "end": v(-83.22, 30.17) * mm});
            skLineSegment(sketch, "E55.top", {"start": v(-79.72, 45.17) * mm, "end": v(-83.22, 45.17) * mm});
            skLineSegment(sketch, "E55.right", {"start": v(-83.22, 30.17) * mm, "end": v(-83.22, 45.17) * mm});
            skSolve(sketch);
        }
        {
            var Q0;
            Q0=makeQuery(id+"F32.imprint","IMPRINT",FACE,{"disambiguationData":[TD([[makeQuery(id+"F32.imprint","IMPRINT",EDGE,{"derivedFrom":sQuery(id+"F32.wireOp",EDGE,"E42.bottom")}),1.0]])]});
            extrude(context, id + "F33", {"entities" : qUnion([Q0]), "depth" : 5 * mm, "offsetDistance" : 25 * mm});
        }
        {
            var Q0;
            Q0=makeQuery(id+"F32.imprint","IMPRINT",FACE,{"disambiguationData":[TD([[makeQuery(id+"F32.imprint","IMPRINT",EDGE,{"derivedFrom":sQuery(id+"F32.wireOp",EDGE,"E44")}),-1.0]])]});
            var Q1;
            Q1=makeQuery(id+"F32.imprint","IMPRINT",FACE,{"disambiguationData":[TD([[makeQuery(id+"F32.imprint","IMPRINT",EDGE,{"derivedFrom":sQuery(id+"F32.wireOp",EDGE,"E43")}),-1.0]])]});
            var Q2;
            Q2=makeQuery(id+"F32.imprint","IMPRINT",FACE,{"disambiguationData":[TD([[makeQuery(id+"F32.imprint","IMPRINT",EDGE,{"derivedFrom":sQuery(id+"F32.wireOp",EDGE,"E45")}),-1.0]])]});
            var Q3;
            Q3=makeQuery(id+"F32.imprint","IMPRINT",FACE,{"disambiguationData":[TD([[makeQuery(id+"F32.imprint","IMPRINT",EDGE,{"derivedFrom":sQuery(id+"F32.wireOp",EDGE,"E46")}),-1.0]])]});
            extrude(context, id + "F34", {"entities" : qUnion([Q0, Q1, Q2, Q3]), "operationType" : NewBodyOperationType.ADD, "depth" : 3 * mm, "offsetDistance" : 25 * mm});
        }
        {
            var Q0;
            {var subQ0=sQuery(id+"F32.wireOp",EDGE,"E53.left");Q0=makeQuery(id+"F32.imprint","IMPRINT",FACE,{"disambiguationData":[TD([[makeQuery(id+"F32.imprint","IMPRINT",EDGE,{"derivedFrom":subQ0}),-1.0]])]});}
            var Q1;
            {var subQ0=sQuery(id+"F32.wireOp",EDGE,"E53.right");Q1=makeQuery(id+"F32.imprint","IMPRINT",FACE,{"disambiguationData":[TD([[makeQuery(id+"F32.imprint","IMPRINT",EDGE,{"derivedFrom":subQ0}),1.0]])]});}
            extrude(context, id + "F35", {"entities" : qUnion([Q0, Q1]), "operationType" : NewBodyOperationType.ADD, "depth" : 5 * mm, "offsetDistance" : 25 * mm});
        }
        {
            var Q0;
            {var subQ0=sQuery(id+"F32.wireOp",EDGE,"E48.right");Q0=makeQuery(id+"F32.imprint","IMPRINT",FACE,{"disambiguationData":[TD([[makeQuery(id+"F32.imprint","IMPRINT",EDGE,{"derivedFrom":subQ0}),1.0]])]});}
            var Q1;
            {var subQ0=sQuery(id+"F32.wireOp",EDGE,"E53.left");Q1=makeQuery(id+"F32.imprint","IMPRINT",FACE,{"disambiguationData":[TD([[makeQuery(id+"F32.imprint","IMPRINT",EDGE,{"derivedFrom":subQ0}),1.0]])]});}
            var Q2;
            {var subQ0=sQuery(id+"F32.wireOp",EDGE,"E48.left");Q2=makeQuery(id+"F32.imprint","IMPRINT",FACE,{"disambiguationData":[TD([[makeQuery(id+"F32.imprint","IMPRINT",EDGE,{"derivedFrom":subQ0}),-1.0]])]});}
            extrude(context, id + "F36", {"entities" : qUnion([Q0, Q1, Q2]), "operationType" : NewBodyOperationType.ADD, "depth" : 18 * mm, "offsetDistance" : 25 * mm});
        }
        {
            var Q0;
            Q0=makeQuery(id+"F36.opExtrude","SWEPT_FACE",FACE,{"disambiguationData":[OSD([sQuery(id+"F32.wireOp",EDGE,"E48.left")])]});
            var sketch = newSketch(context, id + "F37", { "sketchPlane" : qUnion([Q0])});
            skCircle(sketch, "E56", {"center": v(-37.67, 12.5) * mm, "radius": 1.6 * mm});
            skPoint(sketch, "E56.centerSnap0", {"position": v(-37.67, 18) * mm});
            skSolve(sketch);
        }
        {
            var Q0;
            Q0 = qSketchRegion(id + "F37", true);
            extrude(context, id + "F38", {"entities" : qUnion([Q0]), "operationType" : NewBodyOperationType.REMOVE, "oppositeDirection" : true, "depth" : 25 * mm, "offsetDistance" : 25 * mm});
        }
        {
            var Q0;
            Q0=qCreatedBy(makeId("Top.planeOp"),FACE);
            var sketch = newSketch(context, id + "F39", { "sketchPlane" : qUnion([Q0])});
            skCircle(sketch, "E57", {"center": v(-98.24, -19.48) * mm, "radius": 15.25 * mm});
            skCircle(sketch, "E58", {"center": v(-98.24, -19.48) * mm, "radius": 19.25 * mm});
            skLineSegment(sketch, "E59.bottom", {"start": v(-95.74, -5.14) * mm, "end": v(-100.74, -5.14) * mm});
            skLineSegment(sketch, "E59.top", {"start": v(-95.74, 0.93) * mm, "end": v(-100.74, 0.93) * mm});
            skLineSegment(sketch, "E59.left", {"start": v(-95.74, -5.14) * mm, "end": v(-95.74, 0.93) * mm});
            skLineSegment(sketch, "E59.right", {"start": v(-100.74, -5.14) * mm, "end": v(-100.74, 0.93) * mm});
            skPoint(sketch, "E59.middle", {"position": v(-98.24, -2.1) * mm});
            skLineSegment(sketch, "E60.bottom", {"start": v(-100.74, -2.1) * mm, "end": v(-104.74, -2.1) * mm});
            skLineSegment(sketch, "E60.top", {"start": v(-100.74, 10.9) * mm, "end": v(-104.74, 10.9) * mm});
            skLineSegment(sketch, "E60.left", {"start": v(-100.74, -2.1) * mm, "end": v(-100.74, 10.9) * mm});
            skLineSegment(sketch, "E60.right", {"start": v(-104.74, -2.1) * mm, "end": v(-104.74, 10.9) * mm});
            skLineSegment(sketch, "E61.bottom", {"start": v(-95.74, -2.1) * mm, "end": v(-91.74, -2.1) * mm});
            skLineSegment(sketch, "E61.top", {"start": v(-95.74, 10.9) * mm, "end": v(-91.74, 10.9) * mm});
            skLineSegment(sketch, "E61.left", {"start": v(-95.74, -2.1) * mm, "end": v(-95.74, 10.9) * mm});
            skLineSegment(sketch, "E61.right", {"start": v(-91.74, -2.1) * mm, "end": v(-91.74, 10.9) * mm});
            skLineSegment(sketch, "E62.bottom", {"start": v(-100.04, -34.62) * mm, "end": v(-103.64, -34.62) * mm});
            skLineSegment(sketch, "E62.top", {"start": v(-100.04, -59.62) * mm, "end": v(-103.64, -59.62) * mm});
            skLineSegment(sketch, "E62.left", {"start": v(-100.04, -34.62) * mm, "end": v(-100.04, -59.62) * mm});
            skLineSegment(sketch, "E62.right", {"start": v(-103.64, -34.62) * mm, "end": v(-103.64, -59.62) * mm});
            skLineSegment(sketch, "E63.bottom", {"start": v(-96.44, -34.62) * mm, "end": v(-92.84, -34.62) * mm});
            skLineSegment(sketch, "E63.top", {"start": v(-96.44, -59.62) * mm, "end": v(-92.84, -59.62) * mm});
            skLineSegment(sketch, "E63.left", {"start": v(-96.44, -34.62) * mm, "end": v(-96.44, -59.62) * mm});
            skLineSegment(sketch, "E63.right", {"start": v(-92.84, -34.62) * mm, "end": v(-92.84, -59.62) * mm});
            skSolve(sketch);
        }
        {
            var Q0;
            {var subQ4=sQuery(id+"F39.wireOp",EDGE,"E61.top");Q0=makeQuery(id+"F39.imprint","IMPRINT",FACE,{"disambiguationData":[TD([[makeQuery(id+"F39.imprint","IMPRINT",EDGE,{"derivedFrom":subQ4}),-1.0]])]});}
            var Q1;
            {var subQ2=sQuery(id+"F39.wireOp",EDGE,"E60.top");Q1=makeQuery(id+"F39.imprint","IMPRINT",FACE,{"disambiguationData":[TD([[makeQuery(id+"F39.imprint","IMPRINT",EDGE,{"derivedFrom":subQ2}),1.0]])]});}
            var Q2;
            {var subQ5=sQuery(id+"F39.wireOp",EDGE,"E60.bottom");Q2=makeQuery(id+"F39.imprint","IMPRINT",FACE,{"disambiguationData":[TD([[makeQuery(id+"F39.imprint","IMPRINT",EDGE,{"derivedFrom":subQ5}),-1.0]])]});}
            var Q3;
            {var subQ0=sQuery(id+"F39.wireOp",EDGE,"E60.bottom");Q3=makeQuery(id+"F39.imprint","IMPRINT",FACE,{"disambiguationData":[TD([[makeQuery(id+"F39.imprint","IMPRINT",EDGE,{"derivedFrom":subQ0}),1.0]])]});}
            var Q4;
            {var subQ0=sQuery(id+"F39.wireOp",EDGE,"E61.bottom");Q4=makeQuery(id+"F39.imprint","IMPRINT",FACE,{"disambiguationData":[TD([[makeQuery(id+"F39.imprint","IMPRINT",EDGE,{"derivedFrom":subQ0}),-1.0]])]});}
            var Q5;
            {var subQ5=sQuery(id+"F39.wireOp",EDGE,"E61.bottom");Q5=makeQuery(id+"F39.imprint","IMPRINT",FACE,{"disambiguationData":[TD([[makeQuery(id+"F39.imprint","IMPRINT",EDGE,{"derivedFrom":subQ5}),1.0]])]});}
            var Q6;
            {var subQ5=sQuery(id+"F39.wireOp",EDGE,"E63.bottom");Q6=makeQuery(id+"F39.imprint","IMPRINT",FACE,{"disambiguationData":[TD([[makeQuery(id+"F39.imprint","IMPRINT",EDGE,{"derivedFrom":subQ5}),-1.0]])]});}
            var Q7;
            {var subQ5=sQuery(id+"F39.wireOp",EDGE,"E63.top");Q7=makeQuery(id+"F39.imprint","IMPRINT",FACE,{"disambiguationData":[TD([[makeQuery(id+"F39.imprint","IMPRINT",EDGE,{"derivedFrom":subQ5}),1.0]])]});}
            var Q8;
            {var subQ5=sQuery(id+"F39.wireOp",EDGE,"E62.bottom");Q8=makeQuery(id+"F39.imprint","IMPRINT",FACE,{"disambiguationData":[TD([[makeQuery(id+"F39.imprint","IMPRINT",EDGE,{"derivedFrom":subQ5}),1.0]])]});}
            var Q9;
            {var subQ5=sQuery(id+"F39.wireOp",EDGE,"E62.top");Q9=makeQuery(id+"F39.imprint","IMPRINT",FACE,{"disambiguationData":[TD([[makeQuery(id+"F39.imprint","IMPRINT",EDGE,{"derivedFrom":subQ5}),-1.0]])]});}
            var Q10;
            {var subQ0=sQuery(id+"F39.wireOp",EDGE,"E62.left");var subQ5=sQuery(id+"F39.wireOp",EDGE,"E58");var subQ6=makeQuery(id+"F39.imprint","INTERSECT",VERTEX,{"derivedFrom":[subQ5,subQ0]});Q10=makeQuery(id+"F39.imprint","IMPRINT",FACE,{"disambiguationData":[TD([[makeQuery(id+"F39.imprint","IMPRINT",EDGE,{"disambiguationData":[TD([[subQ6,-1.0]])],"derivedFrom":subQ5}),1.0]])]});}
            extrude(context, id + "F40", {"entities" : qUnion([Q0, Q1, Q2, Q3, Q4, Q5, Q6, Q7, Q8, Q9, Q10]), "depth" : 20 * mm, "offsetDistance" : 25 * mm});
        }
        {
            var Q0;
            Q0=makeQuery(id+"F40.opExtrude","SWEPT_FACE",FACE,{"disambiguationData":[OSD([sQuery(id+"F39.wireOp",EDGE,"E62.right")])]});
            var sketch = newSketch(context, id + "F41", { "sketchPlane" : qUnion([Q0])});
            skCircle(sketch, "E64", {"center": v(48.79, 10) * mm, "radius": 2.15 * mm});
            skPoint(sketch, "E64.centerSnap0", {"position": v(48.79, 20) * mm});
            skPoint(sketch, "E64.centerSnap1", {"position": v(59.62, 10) * mm});
            skSolve(sketch);
        }
        {
            var Q0;
            Q0=makeQuery(id+"F41.imprint","IMPRINT",FACE,{"disambiguationData":[TD([[makeQuery(id+"F41.imprint","IMPRINT",EDGE,{"derivedFrom":sQuery(id+"F41.wireOp",EDGE,"E64")}),1.0]])]});
            extrude(context, id + "F42", {"entities" : qUnion([Q0]), "operationType" : NewBodyOperationType.REMOVE, "oppositeDirection" : true, "depth" : 25 * mm, "offsetDistance" : 25 * mm});
        }
        {
            var Q0;
            Q0=makeQuery(id+"F40.opExtrude","SWEPT_FACE",FACE,{"disambiguationData":[OSD([sQuery(id+"F39.wireOp",EDGE,"E60.right")])]});
            var sketch = newSketch(context, id + "F43", { "sketchPlane" : qUnion([Q0])});
            skCircle(sketch, "E65", {"center": v(-4.77, 10) * mm, "radius": 1.6 * mm});
            skPoint(sketch, "E65.centerSnap0", {"position": v(-4.77, 20) * mm});
            skPoint(sketch, "E65.centerSnap1", {"position": v(-10.9, 10) * mm});
            skSolve(sketch);
        }
        {
            var Q0;
            Q0=makeQuery(id+"F43.imprint","IMPRINT",FACE,{"disambiguationData":[TD([[makeQuery(id+"F43.imprint","IMPRINT",EDGE,{"derivedFrom":sQuery(id+"F43.wireOp",EDGE,"E65")}),1.0]])]});
            extrude(context, id + "F44", {"entities" : qUnion([Q0]), "operationType" : NewBodyOperationType.REMOVE, "oppositeDirection" : true, "depth" : 25 * mm, "offsetDistance" : 25 * mm});
        }
        {
            var Q0;
            Q0=makeQuery(id+"F40.opExtrude","CAP_EDGE",EDGE,{"disambiguationData":[OSD([sQuery(id+"F39.wireOp",EDGE,"E62.top")])],"isStart":false});
            var Q1;
            Q1=makeQuery(id+"F40.opExtrude","CAP_EDGE",EDGE,{"disambiguationData":[OSD([sQuery(id+"F39.wireOp",EDGE,"E63.top")])],"isStart":false});
            var Q2;
            Q2=makeQuery(id+"F40.opExtrude","CAP_EDGE",EDGE,{"disambiguationData":[OSD([sQuery(id+"F39.wireOp",EDGE,"E62.top")])],"isStart":true});
            var Q3;
            Q3=makeQuery(id+"F40.opExtrude","CAP_EDGE",EDGE,{"disambiguationData":[OSD([sQuery(id+"F39.wireOp",EDGE,"E63.top")])],"isStart":true});
            var Q4;
            Q4=makeQuery(id+"F40.opExtrude","CAP_EDGE",EDGE,{"disambiguationData":[OSD([sQuery(id+"F39.wireOp",EDGE,"E60.top")])],"isStart":false});
            var Q5;
            Q5=makeQuery(id+"F40.opExtrude","CAP_EDGE",EDGE,{"disambiguationData":[OSD([sQuery(id+"F39.wireOp",EDGE,"E61.top")])],"isStart":false});
            var Q6;
            Q6=makeQuery(id+"F40.opExtrude","CAP_EDGE",EDGE,{"disambiguationData":[OSD([sQuery(id+"F39.wireOp",EDGE,"E61.top")])],"isStart":true});
            var Q7;
            Q7=makeQuery(id+"F40.opExtrude","CAP_EDGE",EDGE,{"disambiguationData":[OSD([sQuery(id+"F39.wireOp",EDGE,"E60.top")])],"isStart":true});
            fillet(context, id + "F45", {"entities" : qUnion([Q0, Q1, Q2, Q3, Q4, Q5, Q6, Q7]), "radius" : 9 * mm, "tangentPropagation" : true, "allowEdgeOverflow" : false});
        }
        {
            var Q0;
            {var subQ0=sQuery(id+"F32.wireOp",EDGE,"E48.top");Q0=makeQuery(id+"F36.opExtrude","CAP_EDGE",EDGE,{"disambiguationData":[OSD([subQ0]),TDD([makeQuery(id+"F32.imprint","IMPRINT",EDGE,{"disambiguationData":[TD([[makeQuery(id+"F32.imprint","INTERSECT",VERTEX,{"derivedFrom":[subQ0,sQuery(id+"F32.wireOp",EDGE,"E48.left")]}),-1.0]])],"derivedFrom":subQ0})])],"isStart":false});}
            var Q1;
            {var subQ0=sQuery(id+"F32.wireOp",EDGE,"E48.top");Q1=makeQuery(id+"F36.opExtrude","CAP_EDGE",EDGE,{"disambiguationData":[OSD([subQ0]),TDD([makeQuery(id+"F32.imprint","IMPRINT",EDGE,{"disambiguationData":[TD([[makeQuery(id+"F32.imprint","INTERSECT",VERTEX,{"derivedFrom":[subQ0,sQuery(id+"F32.wireOp",EDGE,"E53.left")]}),1.0]])],"derivedFrom":subQ0})])],"isStart":false});}
            var Q2;
            {var subQ0=sQuery(id+"F32.wireOp",EDGE,"E48.top");Q2=makeQuery(id+"F36.opExtrude","CAP_EDGE",EDGE,{"disambiguationData":[OSD([subQ0]),TDD([makeQuery(id+"F32.imprint","IMPRINT",EDGE,{"disambiguationData":[TD([[makeQuery(id+"F32.imprint","INTERSECT",VERTEX,{"derivedFrom":[subQ0,sQuery(id+"F32.wireOp",EDGE,"E48.right")]}),1.0]])],"derivedFrom":subQ0})])],"isStart":false});}
            var Q3;
            {var subQ0=sQuery(id+"F32.wireOp",EDGE,"E48.bottom");Q3=makeQuery(id+"F36.opExtrude","CAP_EDGE",EDGE,{"disambiguationData":[OSD([subQ0]),TDD([makeQuery(id+"F32.imprint","IMPRINT",EDGE,{"disambiguationData":[TD([[makeQuery(id+"F32.imprint","INTERSECT",VERTEX,{"derivedFrom":[subQ0,sQuery(id+"F32.wireOp",EDGE,"E48.right")]}),1.0]])],"derivedFrom":subQ0})])],"isStart":false});}
            var Q4;
            {var subQ0=sQuery(id+"F32.wireOp",EDGE,"E48.bottom");Q4=makeQuery(id+"F36.opExtrude","CAP_EDGE",EDGE,{"disambiguationData":[OSD([subQ0]),TDD([makeQuery(id+"F32.imprint","IMPRINT",EDGE,{"disambiguationData":[TD([[makeQuery(id+"F32.imprint","INTERSECT",VERTEX,{"derivedFrom":[subQ0,sQuery(id+"F32.wireOp",EDGE,"E53.left")]}),1.0]])],"derivedFrom":subQ0})])],"isStart":false});}
            var Q5;
            {var subQ0=sQuery(id+"F32.wireOp",EDGE,"E48.bottom");Q5=makeQuery(id+"F36.opExtrude","CAP_EDGE",EDGE,{"disambiguationData":[OSD([subQ0]),TDD([makeQuery(id+"F32.imprint","IMPRINT",EDGE,{"disambiguationData":[TD([[makeQuery(id+"F32.imprint","INTERSECT",VERTEX,{"derivedFrom":[subQ0,sQuery(id+"F32.wireOp",EDGE,"E48.left")]}),-1.0]])],"derivedFrom":subQ0})])],"isStart":false});}
            fillet(context, id + "F46", {"entities" : qUnion([Q0, Q1, Q2, Q3, Q4, Q5]), "radius" : 7 * mm, "tangentPropagation" : true, "allowEdgeOverflow" : false});
        }
        {
            var Q0;
            Q0=makeQuery(id+"F33.opExtrude","SWEPT_EDGE",EDGE,{"disambiguationData":[OSD([sQuery(id+"F32.wireOp",EDGE,"E42.bottom"),sQuery(id+"F32.wireOp",EDGE,"E42.left")])]});
            var Q1;
            Q1=makeQuery(id+"F33.opExtrude","SWEPT_EDGE",EDGE,{"disambiguationData":[OSD([sQuery(id+"F32.wireOp",EDGE,"E42.bottom"),sQuery(id+"F32.wireOp",EDGE,"E42.right")])]});
            var Q2;
            Q2=makeQuery(id+"F33.opExtrude","SWEPT_EDGE",EDGE,{"disambiguationData":[OSD([sQuery(id+"F32.wireOp",EDGE,"E42.top"),sQuery(id+"F32.wireOp",EDGE,"E42.right")])]});
            var Q3;
            Q3=makeQuery(id+"F33.opExtrude","SWEPT_EDGE",EDGE,{"disambiguationData":[OSD([sQuery(id+"F32.wireOp",EDGE,"E42.top"),sQuery(id+"F32.wireOp",EDGE,"E42.left")])]});
            fillet(context, id + "F47", {"entities" : qUnion([Q0, Q1, Q2, Q3]), "radius" : 3 * mm, "tangentPropagation" : true, "allowEdgeOverflow" : false});
        }
    });
